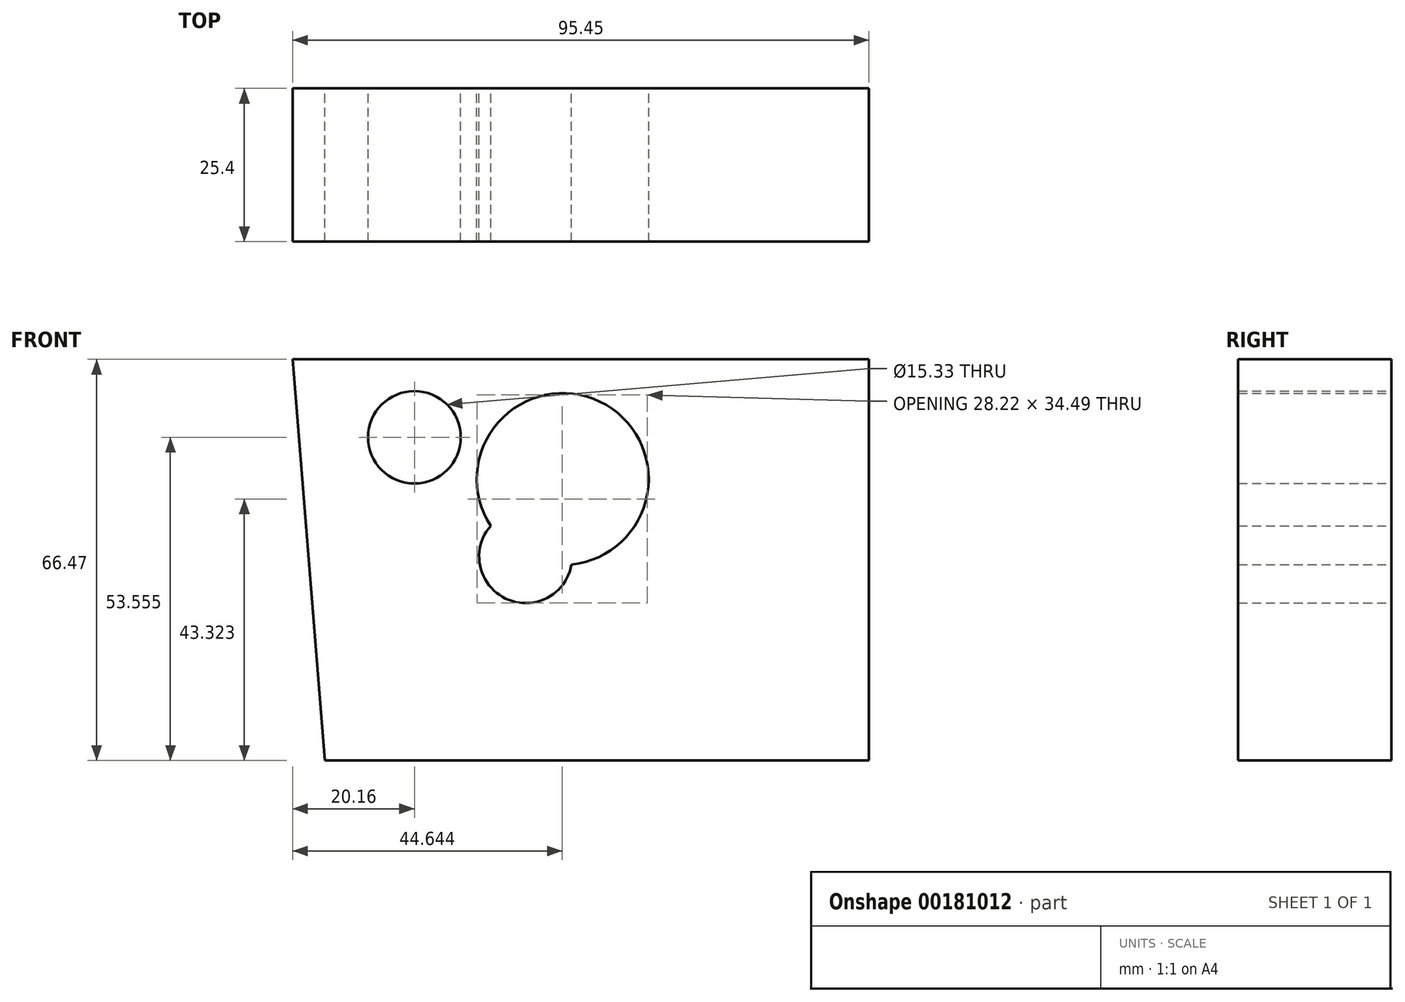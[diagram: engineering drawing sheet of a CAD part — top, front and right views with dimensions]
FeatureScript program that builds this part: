
annotation { "Feature Type Name" : "Feature", "Feature Type Description" : "" }
export const myFeature = defineFeature(function(context is Context, id is Id, definition is map)
    precondition{}
    {
        {
            var Q0;
            Q0=qCreatedBy(makeId("Front.planeOp"),FACE);
            var sketch = newSketch(context, id + "F0", { "sketchPlane" : qUnion([Q0])});
            skLineSegment(sketch, "E0", {"start": v(-54.18, 42.2) * mm, "end": v(41.27, 42.2) * mm});
            skLineSegment(sketch, "E1", {"start": v(41.27, 42.2) * mm, "end": v(41.27, -24.26) * mm});
            skLineSegment(sketch, "E2", {"start": v(41.27, -24.26) * mm, "end": v(-48.82, -24.26) * mm});
            skLineSegment(sketch, "E3", {"start": v(-48.82, -24.26) * mm, "end": v(-54.18, 42.2) * mm});
            skCircle(sketch, "E4", {"center": v(-34.02, 29.3) * mm, "radius": 7.66 * mm});
            skCircle(sketch, "E5", {"center": v(-9.45, 22.36) * mm, "radius": 14.23 * mm});
            skCircle(sketch, "E6", {"center": v(-15.59, 9.53) * mm, "radius": 7.7 * mm});
            skSolve(sketch);
        }
        {
            var Q0;
            Q0=makeQuery(id+"F0.imprint","IMPRINT",FACE,{"disambiguationData":[TD([[makeQuery(id+"F0.imprint","IMPRINT",EDGE,{"derivedFrom":sQuery(id+"F0.wireOp",EDGE,"E0")}),-1.0]])]});
            extrude(context, id + "F1", {"entities" : qUnion([Q0]), "depth" : 25.4 * mm});
        }
    });
